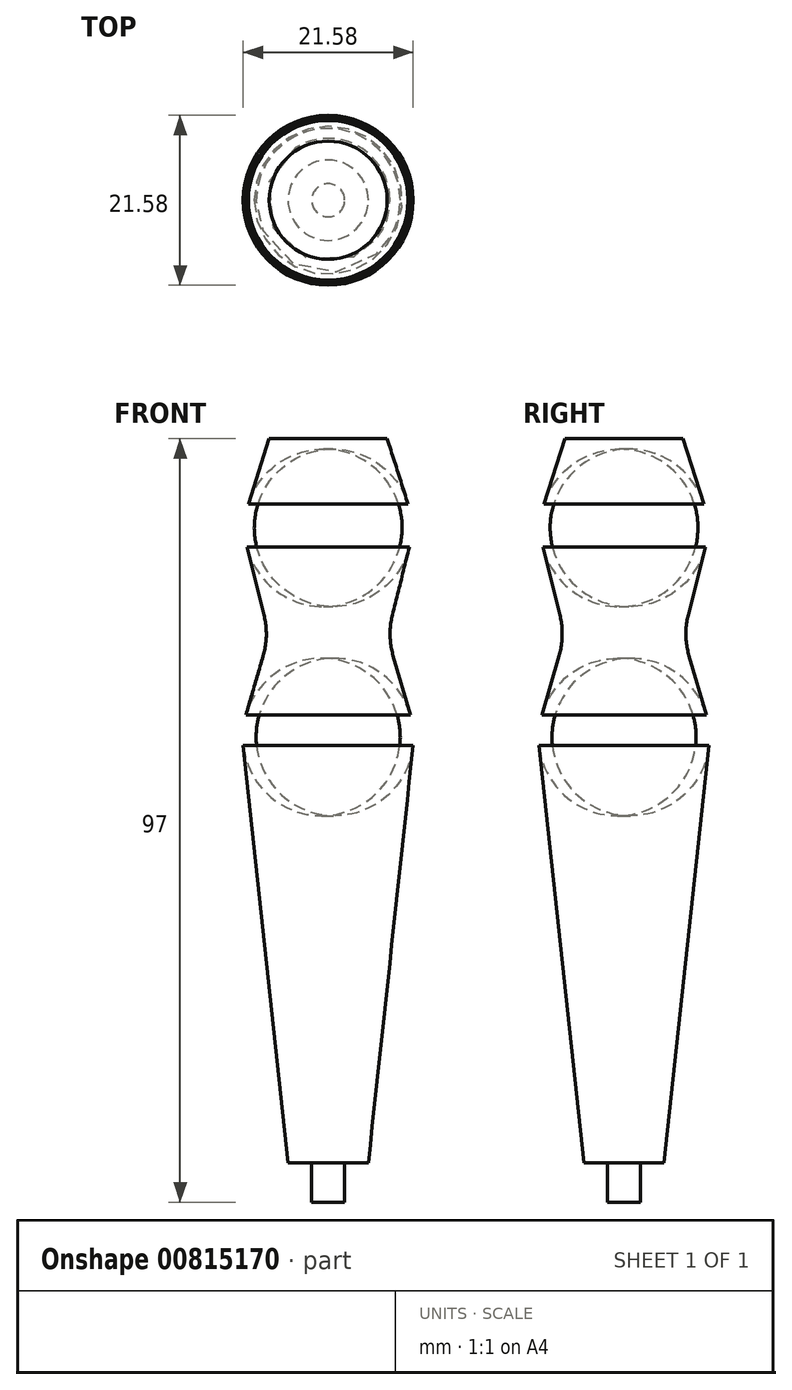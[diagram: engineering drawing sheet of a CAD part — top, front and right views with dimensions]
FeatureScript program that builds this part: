
annotation { "Feature Type Name" : "Feature", "Feature Type Description" : "" }
export const myFeature = defineFeature(function(context is Context, id is Id, definition is map)
    precondition{}
    {
        {
            var Q0;
            Q0=qCreatedBy(makeId("Front.planeOp"),FACE);
            var sketch = newSketch(context, id + "F0", { "sketchPlane" : qUnion([Q0])});
            skLineSegment(sketch, "E0", {"start": v(-5.1, 0) * mm, "end": v(-11, 55) * mm});
            skLineSegment(sketch, "E1", {"start": v(-11, 55) * mm, "end": v(-7.5, 67) * mm});
            skLineSegment(sketch, "E2", {"start": v(-7.5, 67) * mm, "end": v(-11, 81) * mm});
            skLineSegment(sketch, "E3", {"start": v(-11, 81) * mm, "end": v(-7.5, 92) * mm});
            skLineSegment(sketch, "E4", {"start": v(-7.5, 92) * mm, "end": v(0, 92) * mm});
            skLineSegment(sketch, "E5", {"start": v(-5.1, 0) * mm, "end": v(-2.1, 0) * mm});
            skLineSegment(sketch, "E6", {"start": v(-2.1, 0) * mm, "end": v(-2.1, -5) * mm});
            skLineSegment(sketch, "E7", {"start": v(0, 0) * mm, "end": v(0, 92) * mm, "construction": true});
            skLineSegment(sketch, "E8", {"start": v(-2.1, -5) * mm, "end": v(0, -5) * mm});
            skLineSegment(sketch, "E9.MirrorCS", {"start": v(2.1, -5) * mm, "end": v(0, -5) * mm});
            skLineSegment(sketch, "E10.MirrorCS", {"start": v(2.1, 0) * mm, "end": v(2.1, -5) * mm});
            skLineSegment(sketch, "E11.MirrorCS", {"start": v(5.1, 0) * mm, "end": v(2.1, 0) * mm});
            skLineSegment(sketch, "E12.MirrorCS", {"start": v(5.1, 0) * mm, "end": v(11, 55) * mm});
            skLineSegment(sketch, "E13.MirrorCS", {"start": v(11, 55) * mm, "end": v(7.5, 67) * mm});
            skLineSegment(sketch, "E14.MirrorCS", {"start": v(7.5, 67) * mm, "end": v(11, 81) * mm});
            skLineSegment(sketch, "E15.MirrorCS", {"start": v(11, 81) * mm, "end": v(7.5, 92) * mm});
            skLineSegment(sketch, "E16.MirrorCS", {"start": v(7.5, 92) * mm, "end": v(0, 92) * mm});
            skLineSegment(sketch, "E17", {"start": v(0, 92) * mm, "end": v(0, -5) * mm});
            skSolve(sketch);
        }
        {
            var Q0;
            Q0=makeQuery(id+"F0.imprint","IMPRINT",FACE,{"disambiguationData":[TD([[makeQuery(id+"F0.imprint","IMPRINT",EDGE,{"derivedFrom":sQuery(id+"F0.wireOp",EDGE,"E0")}),-1.0]])]});
            var Q1;
            Q1=sQuery(id+"F0.wireOp",EDGE,"E17");
            revolve(context, id + "F1", {"surfaceOperationType" : NewSurfaceOperationType.NEW, "entities" : qUnion([Q0]), "axis" : qUnion([Q1]), "revolveType" : RevolveType.FULL});
        }
        {
            var Q0;
            Q0=makeQuery(id+"F1.opRevolve","SWEPT_EDGE",EDGE,{"disambiguationData":[OSD([sQuery(id+"F0.wireOp",EDGE,"E0"),sQuery(id+"F0.wireOp",EDGE,"E1")])]});
            var Q1;
            Q1=makeQuery(id+"F1.opRevolve","SWEPT_EDGE",EDGE,{"disambiguationData":[OSD([sQuery(id+"F0.wireOp",EDGE,"E1"),sQuery(id+"F0.wireOp",EDGE,"E2")])]});
            var Q2;
            Q2=makeQuery(id+"F1.opRevolve","SWEPT_EDGE",EDGE,{"disambiguationData":[OSD([sQuery(id+"F0.wireOp",EDGE,"E2"),sQuery(id+"F0.wireOp",EDGE,"E3")])]});
            fillet(context, id + "F2", {"entities" : qUnion([Q0, Q1, Q2]), "radius" : 10 * mm, "tangentPropagation" : true, "allowEdgeOverflow" : false});
        }
    });
